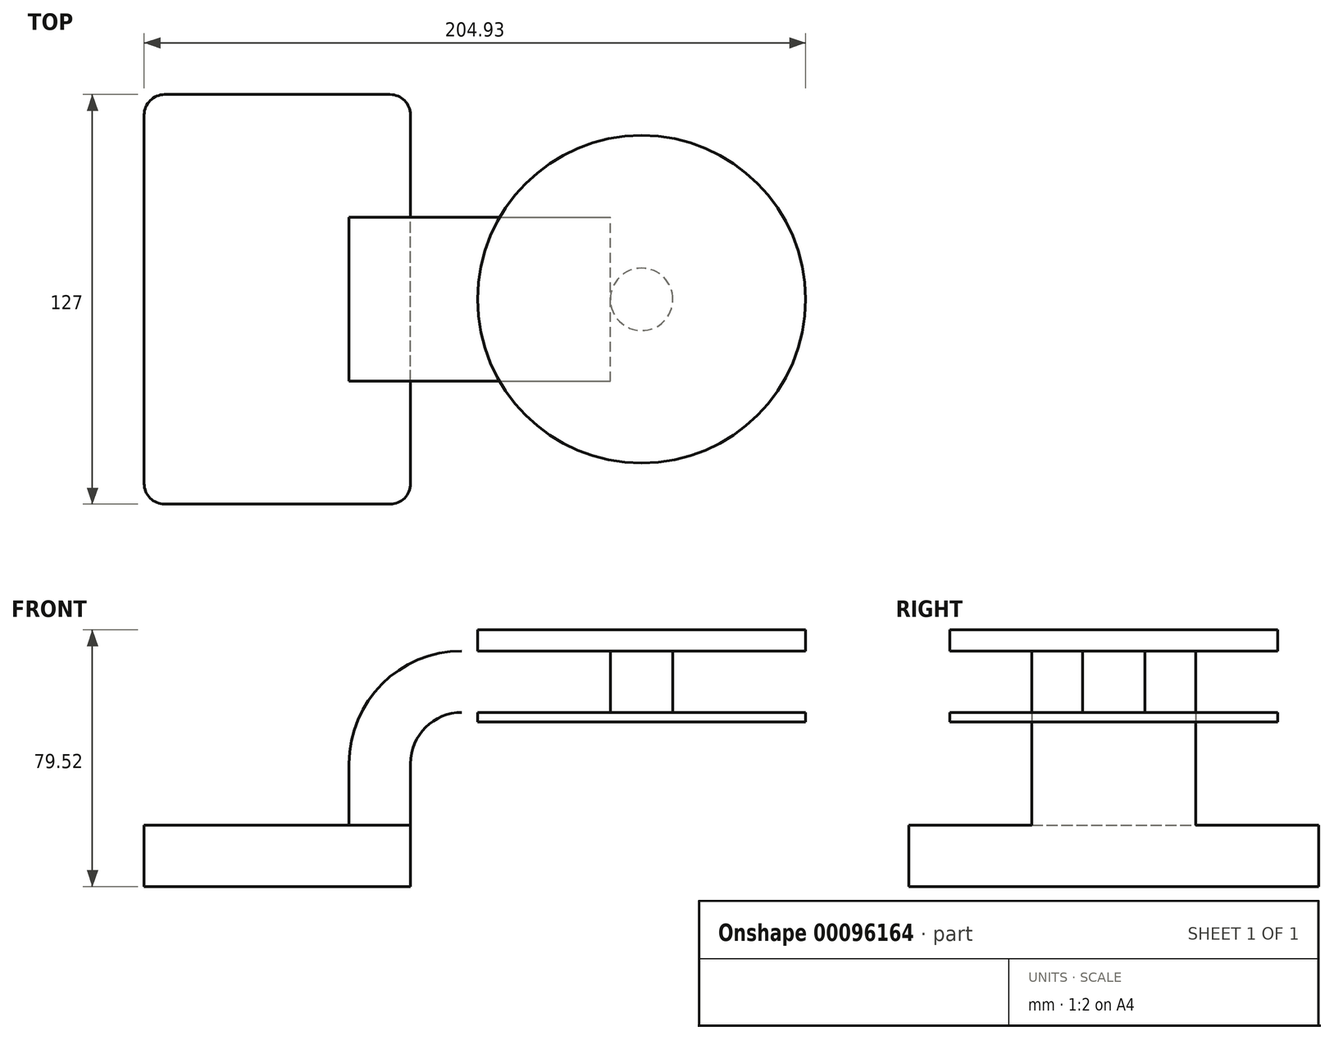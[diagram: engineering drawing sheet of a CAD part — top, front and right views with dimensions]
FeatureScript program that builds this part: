
annotation { "Feature Type Name" : "Feature", "Feature Type Description" : "" }
export const myFeature = defineFeature(function(context is Context, id is Id, definition is map)
    precondition{}
    {
        {
            var Q0;
            Q0=qCreatedBy(makeId("Front.planeOp"),FACE);
            var sketch = newSketch(context, id + "F0", { "sketchPlane" : qUnion([Q0])});
            skLineSegment(sketch, "E0.bottom", {"start": v(-41.28, -9.53) * mm, "end": v(41.28, -9.53) * mm});
            skLineSegment(sketch, "E0.top", {"start": v(-41.28, 9.52) * mm, "end": v(41.27, 9.52) * mm});
            skLineSegment(sketch, "E0.left", {"start": v(-41.27, -9.53) * mm, "end": v(-41.28, 9.52) * mm});
            skLineSegment(sketch, "E0.right", {"start": v(41.28, -9.53) * mm, "end": v(41.27, 9.52) * mm});
            skPoint(sketch, "E0.middle", {"position": v(0, 0) * mm});
            skLineSegment(sketch, "E1.bottom", {"start": v(112.86, 41.42) * mm, "end": v(62.06, 41.42) * mm});
            skLineSegment(sketch, "E1.top", {"start": v(112.86, 70) * mm, "end": v(62.06, 70) * mm});
            skLineSegment(sketch, "E1.left", {"start": v(112.86, 41.42) * mm, "end": v(112.86, 70) * mm});
            skLineSegment(sketch, "E1.right", {"start": v(62.06, 41.42) * mm, "end": v(62.06, 70) * mm});
            skPoint(sketch, "E1.middle", {"position": v(87.46, 55.7) * mm});
            skLineSegment(sketch, "E2", {"start": v(41.27, 9.52) * mm, "end": v(41.27, 28.57) * mm});
            skArc(sketch, "E3", {"start": v(41.27, 28.57) * mm, "mid": v(45.92, 39.8) * mm, "end": v(57.15, 44.45) * mm});
            skLineSegment(sketch, "E4", {"start": v(57.15, 44.45) * mm, "end": v(103.17, 44.45) * mm});
            skLineSegment(sketch, "E5.0", {"start": v(57.15, 63.5) * mm, "end": v(103.17, 63.5) * mm});
            skArc(sketch, "E5.1", {"start": v(22.22, 28.57) * mm, "mid": v(32.45, 53.27) * mm, "end": v(57.15, 63.5) * mm});
            skLineSegment(sketch, "E5.2", {"start": v(22.22, 9.52) * mm, "end": v(22.22, 28.57) * mm});
            skLineSegment(sketch, "E6", {"start": v(103.17, 44.45) * mm, "end": v(103.17, 63.5) * mm});
            skFitSpline(sketch, "E7", {"points": [v(-41.28, 9.52) * mm, v(57.15, 63.5) * mm], "startDerivative": vector(14.82, 159) * mm, "endDerivative": vector(135.67, -7.8) * mm});
            skSolve(sketch);
        }
        {
            var Q0;
            Q0=makeQuery(id+"F0.imprint","IMPRINT",FACE,{"disambiguationData":[TD([[makeQuery(id+"F0.imprint","IMPRINT",EDGE,{"derivedFrom":sQuery(id+"F0.wireOp",EDGE,"E0.bottom")}),1.0]])]});
            extrude(context, id + "F1", {"entities" : qUnion([Q0]), "endBound" : BoundingType.SYMMETRIC, "depth" : 127 * mm});
        }
        {
            var Q0;
            {var subQ1=sQuery(id+"F0.wireOp",EDGE,"E2");Q0=makeQuery(id+"F0.imprint","IMPRINT",FACE,{"disambiguationData":[TD([[makeQuery(id+"F0.imprint","IMPRINT",EDGE,{"derivedFrom":subQ1}),1.0]])]});}
            var Q1;
            {var subQ5=sQuery(id+"F0.wireOp",EDGE,"E6");Q1=makeQuery(id+"F0.imprint","IMPRINT",FACE,{"disambiguationData":[TD([[makeQuery(id+"F0.imprint","IMPRINT",EDGE,{"derivedFrom":subQ5}),1.0]])]});}
            extrude(context, id + "F2", {"entities" : qUnion([Q0, Q1]), "operationType" : NewBodyOperationType.ADD, "endBound" : BoundingType.SYMMETRIC, "depth" : 50.8 * mm});
        }
        {
            var Q0;
            Q0=makeQuery(id+"F0.imprint","IMPRINT",FACE,{"disambiguationData":[TD([[makeQuery(id+"F0.imprint","IMPRINT",EDGE,{"derivedFrom":sQuery(id+"F0.wireOp",EDGE,"E5.1")}),1.0]])]});
            extrude(context, id + "F3", {"entities" : qUnion([Q0]), "operationType" : NewBodyOperationType.ADD, "endBound" : BoundingType.SYMMETRIC, "depth" : 15.88 * mm});
        }
        {
            var Q0;
            {var subQ1=sQuery(id+"F0.wireOp",EDGE,"E1.bottom");Q0=makeQuery(id+"F0.imprint","IMPRINT",FACE,{"disambiguationData":[TD([[makeQuery(id+"F0.imprint","IMPRINT",EDGE,{"derivedFrom":subQ1}),-1.0]])]});}
            var Q1;
            Q1=sQuery(id+"F0.wireOp",EDGE,"E1.left");
            revolve(context, id + "F4", {"entities" : qUnion([Q0]), "axis" : qUnion([Q1]), "revolveType" : RevolveType.FULL});
        }
        {
            var Q0;
            Q0=makeQuery(id+"F1.opExtrude","CAP_EDGE",EDGE,{"disambiguationData":[OSD([sQuery(id+"F0.wireOp",EDGE,"E0.right")])],"isStart":false});
            var Q1;
            Q1=makeQuery(id+"F1.opExtrude","CAP_EDGE",EDGE,{"disambiguationData":[OSD([sQuery(id+"F0.wireOp",EDGE,"E0.left")])],"isStart":false});
            var Q2;
            Q2=makeQuery(id+"F1.opExtrude","CAP_EDGE",EDGE,{"disambiguationData":[OSD([sQuery(id+"F0.wireOp",EDGE,"E0.right")])],"isStart":true});
            var Q3;
            Q3=makeQuery(id+"F1.opExtrude","CAP_EDGE",EDGE,{"disambiguationData":[OSD([sQuery(id+"F0.wireOp",EDGE,"E0.left")])],"isStart":true});
            fillet(context, id + "F5", {"entities" : qUnion([Q0, Q1, Q2, Q3]), "radius" : 6.35 * mm, "tangentPropagation" : true, "allowEdgeOverflow" : false});
        }
    });
